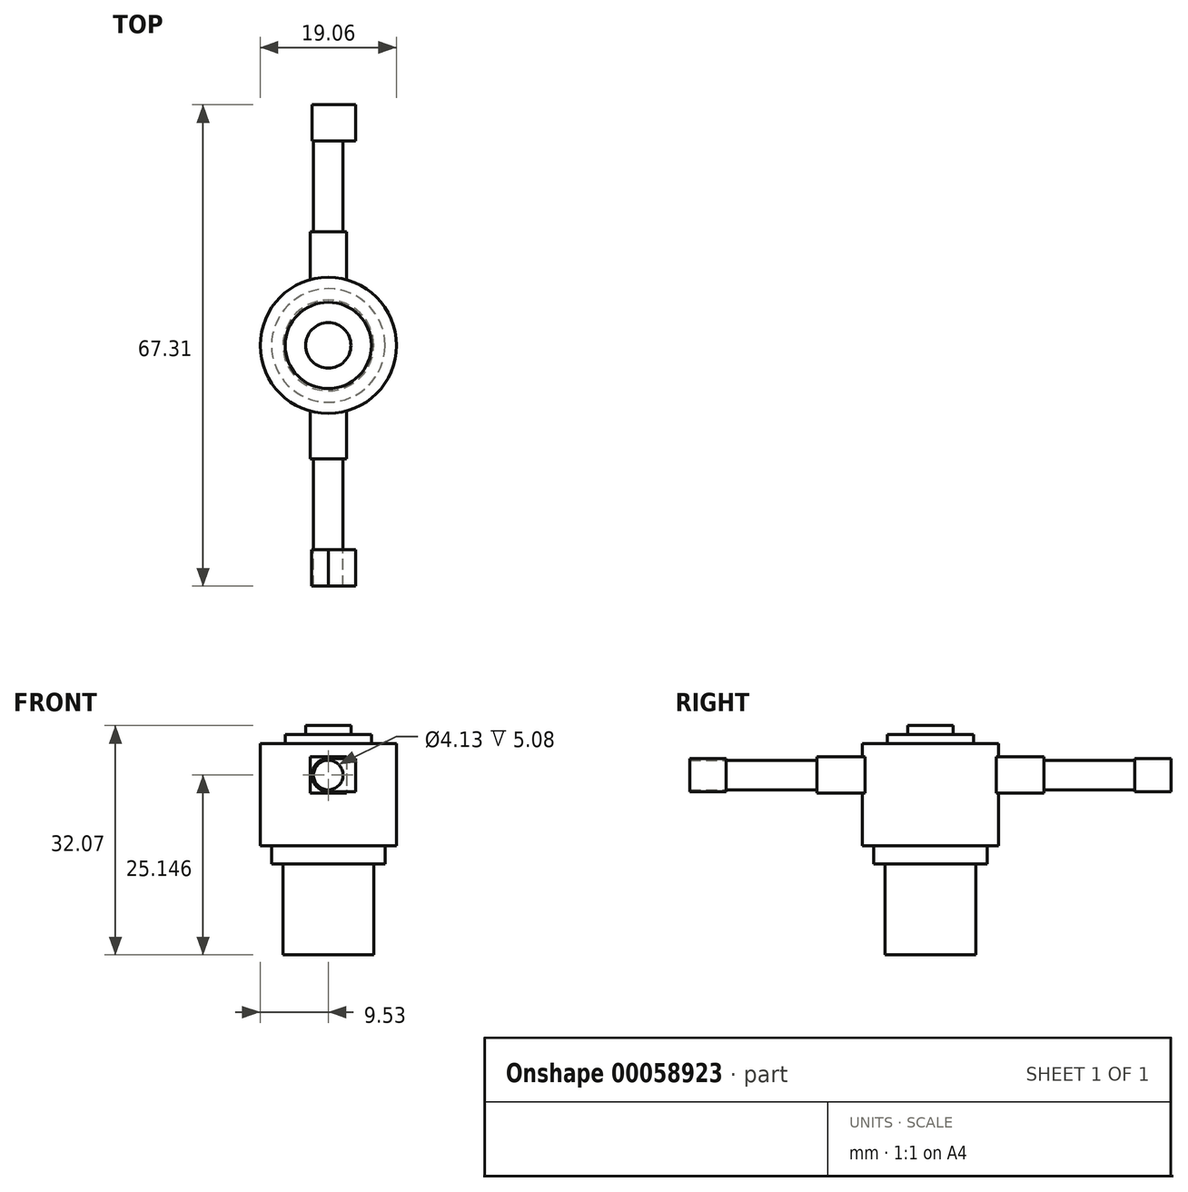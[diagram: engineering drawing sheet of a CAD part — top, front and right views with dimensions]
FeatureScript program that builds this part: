
annotation { "Feature Type Name" : "Feature", "Feature Type Description" : "" }
export const myFeature = defineFeature(function(context is Context, id is Id, definition is map)
    precondition{}
    {
        {
            var Q0;
            Q0=qCreatedBy(makeId("Top.planeOp"),FACE);
            var sketch = newSketch(context, id + "F0", { "sketchPlane" : qUnion([Q0])});
            skCircle(sketch, "E0", {"center": v(0, 0) * mm, "radius": 9.53 * mm});
            skSolve(sketch);
        }
        {
            var Q0;
            Q0=makeQuery(id+"F0.imprint","IMPRINT",FACE,{"disambiguationData":[TD([[makeQuery(id+"F0.imprint","IMPRINT",EDGE,{"derivedFrom":sQuery(id+"F0.wireOp",EDGE,"E0")}),1.0]])]});
            extrude(context, id + "F1", {"entities" : qUnion([Q0]), "depth" : 14.29 * mm});
        }
        {
            var Q0;
            Q0=makeQuery(id+"F1.opExtrude","CAP_FACE",FACE,{"disambiguationData":[OSD([sQuery(id+"F0.wireOp",EDGE,"E0")])],"isStart":false});
            var sketch = newSketch(context, id + "F2", { "sketchPlane" : qUnion([Q0])});
            skCircle(sketch, "E1", {"center": v(0, 0) * mm, "radius": 6.03 * mm});
            skSolve(sketch);
        }
        {
            var Q0;
            Q0 = qSketchRegion(id + "F2", true);
            extrude(context, id + "F3", {"entities" : qUnion([Q0]), "operationType" : NewBodyOperationType.ADD, "depth" : 1.27 * mm});
        }
        {
            var Q0;
            Q0=makeQuery(id+"F3.opExtrude","CAP_FACE",FACE,{"disambiguationData":[OSD([sQuery(id+"F2.wireOp",EDGE,"E1")])],"isStart":false});
            var sketch = newSketch(context, id + "F4", { "sketchPlane" : qUnion([Q0])});
            skCircle(sketch, "E2", {"center": v(0, 0) * mm, "radius": 3.17 * mm});
            skSolve(sketch);
        }
        {
            var Q0;
            Q0 = qSketchRegion(id + "F4", true);
            extrude(context, id + "F5", {"entities" : qUnion([Q0]), "operationType" : NewBodyOperationType.ADD, "depth" : 1.27 * mm});
        }
        {
            var Q0;
            Q0=qCreatedBy(makeId("Top.planeOp"),FACE);
            cPlane(context, id + "F6", {"entities" : qUnion([Q0]), "cplaneType" : CPlaneType.OFFSET, "offset" : 7.37 * mm, "width" : 152.4 * mm, "height" : 152.4 * mm});
        }
        {
            var Q0;
            Q0=qCreatedBy(id+"F6.planeOp",FACE);
            var sketch = newSketch(context, id + "F7", { "sketchPlane" : qUnion([Q0])});
            skLineSegment(sketch, "E3.rect.bottom", {"start": v(2.54, 15.88) * mm, "end": v(-2.54, 15.88) * mm});
            skLineSegment(sketch, "E3.rect.top", {"start": v(2.54, -15.88) * mm, "end": v(-2.54, -15.88) * mm});
            skLineSegment(sketch, "E3.rect.left", {"start": v(2.54, -15.88) * mm, "end": v(2.54, 15.88) * mm});
            skLineSegment(sketch, "E3.rect.right", {"start": v(-2.54, -15.88) * mm, "end": v(-2.54, 15.88) * mm});
            skPoint(sketch, "E3.rect.middle", {"position": v(0, 0) * mm});
            skSolve(sketch);
        }
        {
            var Q0;
            Q0=makeQuery(id+"F7.imprint","IMPRINT",FACE,{"disambiguationData":[TD([[makeQuery(id+"F7.imprint","IMPRINT",EDGE,{"derivedFrom":sQuery(id+"F7.wireOp",EDGE,"E3.rect.bottom")}),1.0]])]});
            extrude(context, id + "F8", {"entities" : qUnion([Q0]), "operationType" : NewBodyOperationType.ADD, "depth" : 5.08 * mm});
        }
        {
            var Q0;
            Q0=makeQuery(id+"F8.opExtrude","SWEPT_FACE",FACE,{"disambiguationData":[OSD([sQuery(id+"F7.wireOp",EDGE,"E3.rect.top")])]});
            var sketch = newSketch(context, id + "F9", { "sketchPlane" : qUnion([Q0])});
            skCircle(sketch, "E4", {"center": v(0, 9.9) * mm, "radius": 2.06 * mm});
            skSolve(sketch);
        }
        {
            var Q0;
            Q0=makeQuery(id+"F9.imprint","IMPRINT",FACE,{"disambiguationData":[TD([[makeQuery(id+"F9.imprint","IMPRINT",EDGE,{"derivedFrom":sQuery(id+"F9.wireOp",EDGE,"E4")}),1.0]])]});
            extrude(context, id + "F10", {"entities" : qUnion([Q0]), "operationType" : NewBodyOperationType.ADD, "depth" : 12.7 * mm});
        }
        {
            var Q0;
            Q0=makeQuery(id+"F10.opExtrude","CAP_FACE",FACE,{"disambiguationData":[OSD([sQuery(id+"F9.wireOp",EDGE,"E4")])],"isStart":false});
            var sketch = newSketch(context, id + "F11", { "sketchPlane" : qUnion([Q0])});
            skLineSegment(sketch, "E5.rect.bottom", {"start": v(0, 12.21) * mm, "end": v(3.8, 12.21) * mm});
            skLineSegment(sketch, "E5.rect.top", {"start": v(0, 7.6) * mm, "end": v(3.81, 7.6) * mm});
            skLineSegment(sketch, "E5.rect.left", {"start": v(0, 12.21) * mm, "end": v(0, 12.2) * mm});
            skLineSegment(sketch, "E5.rect.right", {"start": v(3.8, 12.21) * mm, "end": v(3.81, 7.6) * mm});
            skPoint(sketch, "E5.rect.middle", {"position": v(1.9, 9.9) * mm});
            skArc(sketch, "E6", {"start": v(0, 12.2) * mm, "mid": v(-2.3, 9.9) * mm, "end": v(0, 7.6) * mm});
            skLineSegment(sketch, "E7.trimOffspring", {"start": v(0, 7.6) * mm, "end": v(0, 7.6) * mm});
            skSolve(sketch);
        }
        {
            var Q0;
            Q0=makeQuery(id+"F11.imprint","IMPRINT",FACE,{"disambiguationData":[TD([[makeQuery(id+"F11.imprint","IMPRINT",EDGE,{"derivedFrom":sQuery(id+"F11.wireOp",EDGE,"E5.rect.bottom")}),-1.0]])]});
            extrude(context, id + "F12", {"entities" : qUnion([Q0]), "depth" : 5.08 * mm});
        }
        {
            var Q0;
            Q0=makeQuery(id+"F10.opExtrude","CAP_FACE",FACE,{"disambiguationData":[OSD([sQuery(id+"F9.wireOp",EDGE,"E4")])],"isStart":false});
            extrude(context, id + "F13", {"entities" : qUnion([Q0]), "depth" : 5.08 * mm});
        }
        {
            var Q0;
            Q0=makeQuery(id+"F8.opExtrude","SWEPT_FACE",FACE,{"disambiguationData":[OSD([sQuery(id+"F7.wireOp",EDGE,"E3.rect.bottom")])]});
            var sketch = newSketch(context, id + "F14", { "sketchPlane" : qUnion([Q0])});
            skCircle(sketch, "E8", {"center": v(0, 9.9) * mm, "radius": 2.06 * mm});
            skSolve(sketch);
        }
        {
            var Q0;
            Q0=makeQuery(id+"F14.imprint","IMPRINT",FACE,{"disambiguationData":[TD([[makeQuery(id+"F14.imprint","IMPRINT",EDGE,{"derivedFrom":sQuery(id+"F14.wireOp",EDGE,"E8")}),1.0]])]});
            extrude(context, id + "F15", {"entities" : qUnion([Q0]), "operationType" : NewBodyOperationType.ADD, "depth" : 12.7 * mm});
        }
        {
            var Q0;
            Q0=makeQuery(id+"F15.opExtrude","CAP_FACE",FACE,{"disambiguationData":[OSD([sQuery(id+"F14.wireOp",EDGE,"E8")])],"isStart":false});
            var sketch = newSketch(context, id + "F16", { "sketchPlane" : qUnion([Q0])});
            skSolve(sketch);
        }
        {
            var Q0;
            Q0=makeQuery(id+"F16.imprint","IMPRINT",FACE,{"disambiguationData":[TD([[makeQuery(id+"F16.imprint","IMPRINT",EDGE,{"derivedFrom":makeQuery(id+"F15.opExtrude","CAP_EDGE",EDGE,{"disambiguationData":[OSD([sQuery(id+"F14.wireOp",EDGE,"E8")])],"isStart":false})}),1.0]])]});
            var sketch = newSketch(context, id + "F17", { "sketchPlane" : qUnion([Q0])});
            skArc(sketch, "E9", {"start": v(0, 7.6) * mm, "mid": v(2.3, 9.9) * mm, "end": v(0, 12.2) * mm});
            skLineSegment(sketch, "E10.rect.bottom", {"start": v(0, 12.2) * mm, "end": v(-3.81, 12.2) * mm});
            skLineSegment(sketch, "E10.rect.top", {"start": v(0, 7.6) * mm, "end": v(-3.8, 7.6) * mm});
            skLineSegment(sketch, "E10.rect.right", {"start": v(-3.81, 12.2) * mm, "end": v(-3.8, 7.6) * mm});
            skPoint(sketch, "E10.rect.middle", {"position": v(-1.9, 9.9) * mm});
            skSolve(sketch);
        }
        {
            var Q0;
            Q0=makeQuery(id+"F17.imprint","IMPRINT",FACE,{"disambiguationData":[TD([[makeQuery(id+"F17.imprint","IMPRINT",EDGE,{"derivedFrom":sQuery(id+"F17.wireOp",EDGE,"E9")}),1.0]])]});
            var Q1;
            Q1=makeQuery(id+"F16.imprint","IMPRINT",FACE,{"disambiguationData":[TD([[makeQuery(id+"F16.imprint","IMPRINT",EDGE,{"derivedFrom":makeQuery(id+"F15.opExtrude","CAP_EDGE",EDGE,{"disambiguationData":[OSD([sQuery(id+"F14.wireOp",EDGE,"E8")])],"isStart":false})}),1.0]])]});
            extrude(context, id + "F18", {"entities" : qUnion([Q0, Q1]), "operationType" : NewBodyOperationType.ADD, "depth" : 5.08 * mm});
        }
        {
            var Q0;
            Q0=makeQuery(id+"F1.opExtrude","CAP_FACE",FACE,{"disambiguationData":[OSD([sQuery(id+"F0.wireOp",EDGE,"E0")])],"isStart":true});
            var sketch = newSketch(context, id + "F19", { "sketchPlane" : qUnion([Q0])});
            skCircle(sketch, "E11", {"center": v(0, 0) * mm, "radius": 7.94 * mm});
            skSolve(sketch);
        }
        {
            var Q0;
            Q0=makeQuery(id+"F19.imprint","IMPRINT",FACE,{"disambiguationData":[TD([[makeQuery(id+"F19.imprint","IMPRINT",EDGE,{"derivedFrom":sQuery(id+"F19.wireOp",EDGE,"E11")}),1.0]])]});
            extrude(context, id + "F20", {"entities" : qUnion([Q0]), "operationType" : NewBodyOperationType.ADD, "depth" : 2.54 * mm});
        }
        {
            var Q0;
            Q0=makeQuery(id+"F20.opExtrude","CAP_FACE",FACE,{"disambiguationData":[OSD([sQuery(id+"F19.wireOp",EDGE,"E11")])],"isStart":false});
            var sketch = newSketch(context, id + "F21", { "sketchPlane" : qUnion([Q0])});
            skCircle(sketch, "E12", {"center": v(0, 0) * mm, "radius": 6.35 * mm});
            skSolve(sketch);
        }
        {
            var Q0;
            Q0=makeQuery(id+"F21.imprint","IMPRINT",FACE,{"disambiguationData":[TD([[makeQuery(id+"F21.imprint","IMPRINT",EDGE,{"derivedFrom":sQuery(id+"F21.wireOp",EDGE,"E12")}),1.0]])]});
            extrude(context, id + "F22", {"entities" : qUnion([Q0]), "operationType" : NewBodyOperationType.ADD, "depth" : 12.7 * mm});
        }
    });
